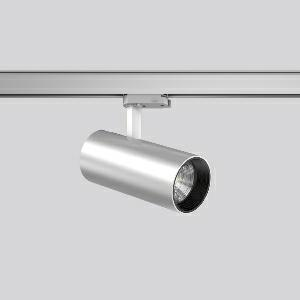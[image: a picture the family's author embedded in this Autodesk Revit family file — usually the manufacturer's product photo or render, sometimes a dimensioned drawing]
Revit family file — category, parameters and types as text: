
# Revit family: deecos_s_mini_742206_004_2_76_cdbd
name_source: partatom
category: Lighting Fixtures
units: mm (PartAtom-declared; Revit-internal decimal feet)

## family parameters
Cut with Voids When Loaded = No
Host = Face
Light Source = No
Part Type = Normal
Room Calculation Point = No
Round Connector Dimension = Use Diameter
Shared = No

## types (1)
- DEECOS S mini (1 x LED Modul 927, 3000 lm, 2700)
    Apparent Load = 29 VA
    Approval mark = CE
    CIE Flux Codes = 99 100 100 100 100
    Color Rendering = 92
    Color Temperature = 2700
    Default Elevation = 1800 mm
    Description = Series: DEECOS S mini
LED surface-mounted projector in modern design with no visible cooling ribs. Housing: die-cast aluminium, powder-coated. Rotation range: 356°. Swivel range: 90°. Black plastic ring and recessed LED to prevent glare from the side. Optical assembly with lens made of plastic (polycarbonate) for the best homogeneous light distribution - can be changed without tools. Best colour rendering index Ra>90. With adapter for RZB 3-circuit DALI tracks. Suitable for Track on ceiling, Wall track. High quality converter without flickering and stroboscopic effect. The following accessories can be mounted without use of tools: interchangeable lenses, decorative glasses, honeycomb louvre, clear and frosted diffusers, white interchangeable plastic ring. 
Colour: silver
Diameter: 87 mm
Height: 214 mm
Lamp: LED
Socket: without socket
Colour temperature: 2700K
Colour rendering index (CRI): 92
System power: 29 W
Rated luminous flux: 3000 lm
Luminous efficiency: 103 lm/W
Control gear: Converter, dimmable, DALI
Protection class: I
Type of protection: IP 20
    Height = 214 mm
    Lamp = 1 x LED Modul 927
    Lamp Light Flux = 3000 lm
    Lamp count = 1
    Length = 87 mm
    Lifetime = 50000 h
    Luminous efficacy = 103 lm/W
    Manufacturer = RZB
    ModVariant = No
    Model = 742206.004.2.76
    Mounting Place = Ceiling
    Mounting Type = Rail mounted
    Number of Poles = 1
    OnlyDefault = Yes
    Power Factor = 1
    Product Name = DEECOS S mini
    Product group = Track mounted projectors
    ProductGroupID = 301
    Protection Class = Protection class I
    Protection Degree = IP 20
    RLX_Detail_Level = 1
    RLX_Emergency_Light_Flux = 0 lm
    RLX_Emergency_Type = 0
    RLX_Emergency_Type_DB = No
    RlxData = <blob elided: 37221 chars, md5=43759203>
    Socket = socket
    Standby Power = 0 W
    System Light Flux = 3000 lm
    System Power = 29 W
    Type Comments = Product without accessories
    Type Image = 741930.004.jpg
    URL = http://relux.com
    VarID = ---
    Voltage = 230 V
    Voltage Range = 220-240 V
    Weight = 0.00 kg
    Width = 0 mm  [stored 0 ft]

note: [stored X ft] marks values corroborated as IEEE doubles in the binary element streams (Revit-internal decimal feet)

## geometry (parser evidence)
native form markers: Blend x4, Sweep x11
no freeform markers — native parametric forms only
